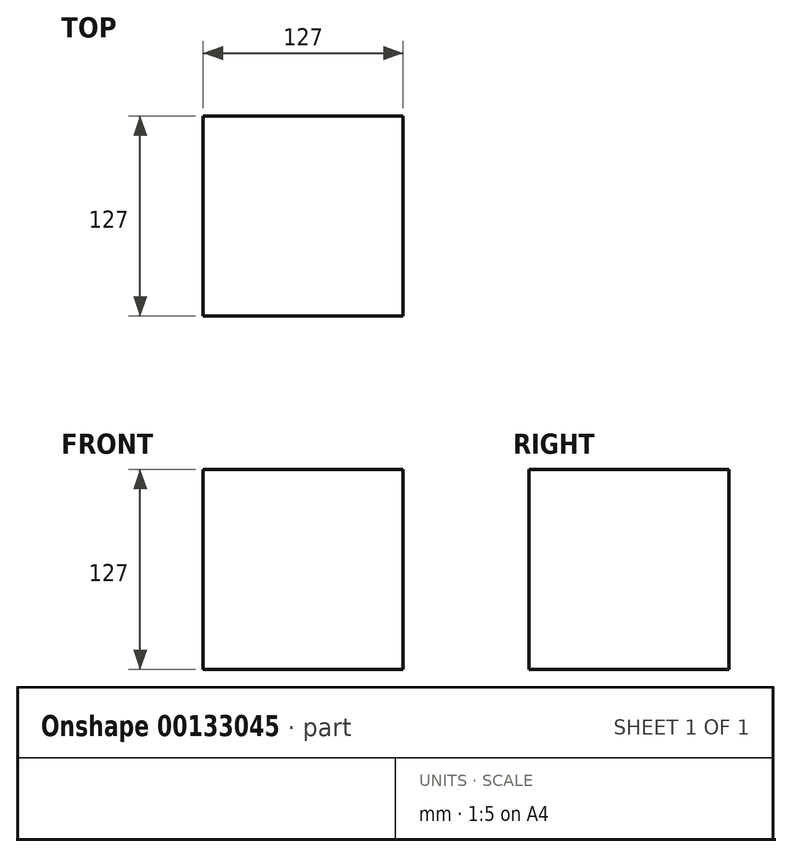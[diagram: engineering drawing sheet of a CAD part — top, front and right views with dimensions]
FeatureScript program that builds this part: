
annotation { "Feature Type Name" : "Feature", "Feature Type Description" : "" }
export const myFeature = defineFeature(function(context is Context, id is Id, definition is map)
    precondition{}
    {
        {
            var Q0;
            Q0=qCreatedBy(makeId("Front.planeOp"),FACE);
            var sketch = newSketch(context, id + "F0", { "sketchPlane" : qUnion([Q0])});
            skLineSegment(sketch, "E0.bottom", {"start": v(-62.05, 65.95) * mm, "end": v(64.95, 65.95) * mm});
            skLineSegment(sketch, "E0.top", {"start": v(-62.05, -61.05) * mm, "end": v(64.95, -61.05) * mm});
            skLineSegment(sketch, "E0.left", {"start": v(-62.05, 65.95) * mm, "end": v(-62.05, -61.05) * mm});
            skLineSegment(sketch, "E0.right", {"start": v(64.95, 65.95) * mm, "end": v(64.95, -61.05) * mm});
            skSolve(sketch);
        }
        {
            var Q0;
            Q0 = qSketchRegion(id + "F0", true);
            extrude(context, id + "F1", {"entities" : qUnion([Q0]), "depth" : 127 * mm});
        }
    });
